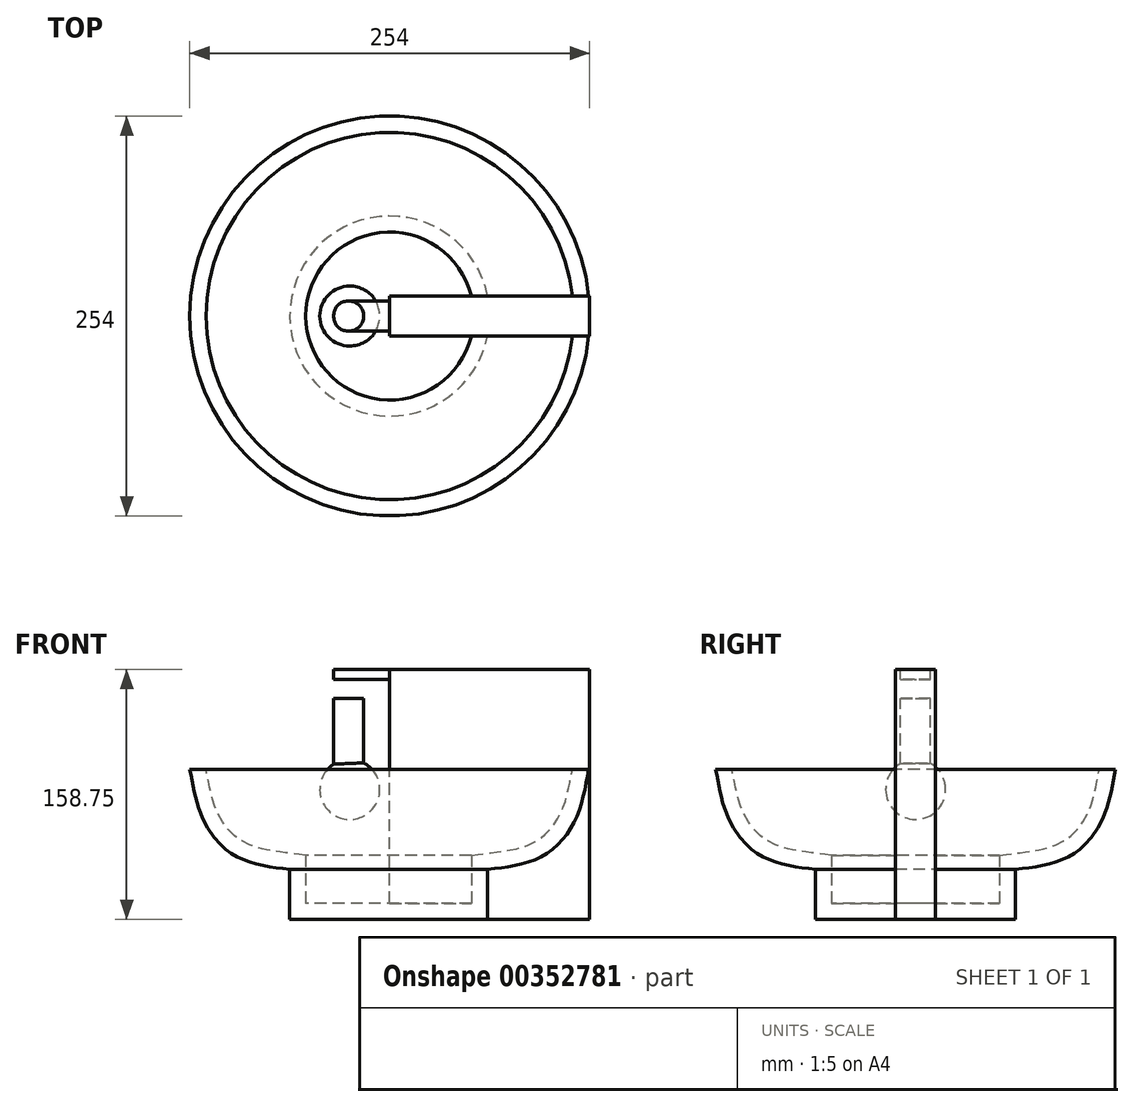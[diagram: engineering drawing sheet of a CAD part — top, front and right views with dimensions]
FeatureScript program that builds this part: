
annotation { "Feature Type Name" : "Feature", "Feature Type Description" : "" }
export const myFeature = defineFeature(function(context is Context, id is Id, definition is map)
    precondition{}
    {
        {
            var Q0;
            Q0=qCreatedBy(makeId("Top.planeOp"),FACE);
            cPlane(context, id + "F0", {"entities" : qUnion([Q0]), "cplaneType" : CPlaneType.OFFSET, "offset" : 95.25 * mm, "oppositeDirection" : true, "width" : 152.4 * mm, "height" : 152.4 * mm});
        }
        {
            var Q0;
            Q0=qCreatedBy(id+"F0.planeOp",FACE);
            var sketch = newSketch(context, id + "F1", { "sketchPlane" : qUnion([Q0])});
            skCircle(sketch, "E0", {"center": v(0, 0) * mm, "radius": 63.5 * mm});
            skSolve(sketch);
        }
        {
            var Q0;
            Q0=qCreatedBy(id+"F0.planeOp",FACE);
            cPlane(context, id + "F2", {"entities" : qUnion([Q0]), "cplaneType" : CPlaneType.OFFSET, "offset" : 31.75 * mm, "width" : 152.4 * mm, "height" : 152.4 * mm});
        }
        {
            var Q0;
            Q0=makeQuery(id+"F1.imprint","IMPRINT",FACE,{"disambiguationData":[TD([[makeQuery(id+"F1.imprint","IMPRINT",EDGE,{"derivedFrom":sQuery(id+"F1.wireOp",EDGE,"E0")}),1.0]])]});
            extrude(context, id + "F3", {"entities" : qUnion([Q0]), "depth" : 31.75 * mm});
        }
        {
            var Q0;
            Q0=qCreatedBy(makeId("Front.planeOp"),FACE);
            var sketch = newSketch(context, id + "F4", { "sketchPlane" : qUnion([Q0])});
            skLineSegment(sketch, "E1", {"start": v(0, 0) * mm, "end": v(0, -63.5) * mm});
            skLineSegment(sketch, "E2", {"start": v(0, -63.5) * mm, "end": v(-63.5, -63.5) * mm});
            skFitSpline(sketch, "E3", {"points": [v(-63.5, -63.5) * mm, v(-97, -55.41) * mm, v(-118.18, -32.67) * mm, v(-127, 0) * mm], "startDerivative": vector(-104.98, 12.82) * mm, "endDerivative": vector(-18.87, 100.94) * mm});
            skLineSegment(sketch, "E4", {"start": v(-127, 0) * mm, "end": v(0, 0) * mm});
            skSolve(sketch);
        }
        {
            var Q0;
            Q0=makeQuery(id+"F4.imprint","IMPRINT",FACE,{"disambiguationData":[TD([[makeQuery(id+"F4.imprint","IMPRINT",EDGE,{"derivedFrom":sQuery(id+"F4.wireOp",EDGE,"E1")}),-1.0]])]});
            var Q1;
            Q1=sQuery(id+"F4.wireOp",EDGE,"E1");
            revolve(context, id + "F5", {"operationType" : NewBodyOperationType.ADD, "entities" : qUnion([Q0]), "axis" : qUnion([Q1]), "revolveType" : RevolveType.FULL});
        }
        {
            var Q0;
            Q0=makeQuery(id+"F5.opRevolve","SWEPT_FACE",FACE,{"disambiguationData":[OSD([sQuery(id+"F4.wireOp",EDGE,"E4")])]});
            shell(context, id + "F6", {"entities" : qUnion([Q0]), "thickness" : 10.16 * mm});
        }
        {
            var Q0;
            Q0=qCreatedBy(makeId("Front.planeOp"),FACE);
            var sketch = newSketch(context, id + "F7", { "sketchPlane" : qUnion([Q0])});
            skLineSegment(sketch, "E5", {"start": v(0, 0) * mm, "end": v(127, 0) * mm});
            skLineSegment(sketch, "E6", {"start": v(127, 0) * mm, "end": v(127, -95.25) * mm});
            skLineSegment(sketch, "E7", {"start": v(127, -95.25) * mm, "end": v(0, -95.25) * mm});
            skLineSegment(sketch, "E8", {"start": v(0, -95.25) * mm, "end": v(0, 0) * mm});
            skSolve(sketch);
        }
        {
            var Q0;
            Q0=makeQuery(id+"F7.imprint","IMPRINT",FACE,{"disambiguationData":[TD([[makeQuery(id+"F7.imprint","IMPRINT",EDGE,{"derivedFrom":sQuery(id+"F7.wireOp",EDGE,"E5")}),-1.0]])]});
            extrude(context, id + "F8", {"entities" : qUnion([Q0]), "operationType" : NewBodyOperationType.ADD, "depth" : 12.7 * mm, "hasSecondDirection" : true, "secondDirectionOppositeDirection" : true, "secondDirectionDepth" : 12.7 * mm});
        }
        {
            var Q0;
            Q0=qCreatedBy(makeId("Top.planeOp"),FACE);
            var sketch = newSketch(context, id + "F9", { "sketchPlane" : qUnion([Q0])});
            skCircle(sketch, "E9", {"center": v(-26.04, 0) * mm, "radius": 9.53 * mm});
            skSolve(sketch);
        }
        {
            var Q0;
            Q0=qCreatedBy(makeId("Front.planeOp"),FACE);
            var sketch = newSketch(context, id + "F10", { "sketchPlane" : qUnion([Q0])});
            skLineSegment(sketch, "E10", {"start": v(0, 78.1) * mm, "end": v(0, -73.87) * mm, "construction": true});
            skLineSegment(sketch, "E11", {"start": v(-25.4, -18.53) * mm, "end": v(-25.4, 44.97) * mm});
            skSolve(sketch);
        }
        {
            var Q0;
            Q0=makeQuery(id+"F9.imprint","IMPRINT",FACE,{"disambiguationData":[TD([[makeQuery(id+"F9.imprint","IMPRINT",EDGE,{"derivedFrom":sQuery(id+"F9.wireOp",EDGE,"E9")}),1.0]])]});
            var Q1;
            Q1=sQuery(id+"F10.wireOp",EDGE,"E11");
            sweep(context, id + "F11", {"profiles" : qUnion([Q0]), "path" : qUnion([Q1])});
        }
        {
            var Q0;
            Q0=qCreatedBy(makeId("Front.planeOp"),FACE);
            var sketch = newSketch(context, id + "F12", { "sketchPlane" : qUnion([Q0])});
            skLineSegment(sketch, "E12", {"start": v(-25.4, 0) * mm, "end": v(-25.4, -25.4) * mm});
            skCircle(sketch, "E13", {"center": v(-25.4, -12.7) * mm, "radius": 19.05 * mm});
            skSolve(sketch);
        }
        {
            var Q0;
            Q0 = qSketchRegion(id + "F12", true);
            extrude(context, id + "F13", {"entities" : qUnion([Q0]), "operationType" : NewBodyOperationType.ADD, "depth" : 19.05 * mm, "hasSecondDirection" : true, "secondDirectionOppositeDirection" : true, "secondDirectionDepth" : 19.05 * mm});
        }
        {
            var Q0;
            Q0=makeQuery(id+"F13.opExtrude","CAP_FACE",FACE,{"disambiguationData":[OSD([sQuery(id+"F12.wireOp",EDGE,"E13")])],"isStart":false});
            fillet(context, id + "F14", {"entities" : qUnion([Q0]), "radius" : 19.05 * mm, "tangentPropagation" : true, "allowEdgeOverflow" : false});
        }
        {
            var Q0;
            Q0=makeQuery(id+"F13.opExtrude","CAP_EDGE",EDGE,{"disambiguationData":[OSD([sQuery(id+"F12.wireOp",EDGE,"E13")])],"isStart":true});
            fillet(context, id + "F15", {"entities" : qUnion([Q0]), "radius" : 19.05 * mm, "tangentPropagation" : true, "allowEdgeOverflow" : false});
        }
        {
            var Q0;
            Q0=qCreatedBy(makeId("Front.planeOp"),FACE);
            var sketch = newSketch(context, id + "F16", { "sketchPlane" : qUnion([Q0])});
            skLineSegment(sketch, "E14", {"start": v(0, 0) * mm, "end": v(0, 63.5) * mm});
            skLineSegment(sketch, "E15", {"start": v(0, 63.5) * mm, "end": v(127, 63.5) * mm});
            skLineSegment(sketch, "E16", {"start": v(127, 63.5) * mm, "end": v(127, 0) * mm});
            skLineSegment(sketch, "E17", {"start": v(127, 0) * mm, "end": v(0, 0) * mm});
            skSolve(sketch);
        }
        {
            var Q0;
            Q0=makeQuery(id+"F16.imprint","IMPRINT",FACE,{"disambiguationData":[TD([[makeQuery(id+"F16.imprint","IMPRINT",EDGE,{"derivedFrom":sQuery(id+"F16.wireOp",EDGE,"E14")}),-1.0]])]});
            extrude(context, id + "F17", {"entities" : qUnion([Q0]), "operationType" : NewBodyOperationType.ADD, "depth" : 12.7 * mm, "hasSecondDirection" : true, "secondDirectionOppositeDirection" : true, "secondDirectionDepth" : 12.7 * mm});
        }
        {
            var Q0;
            Q0=qCreatedBy(makeId("Front.planeOp"),FACE);
            var sketch = newSketch(context, id + "F18", { "sketchPlane" : qUnion([Q0])});
            skLineSegment(sketch, "E18", {"start": v(0, 0) * mm, "end": v(0, 63.5) * mm});
            skLineSegment(sketch, "E19", {"start": v(0, 63.5) * mm, "end": v(-35.56, 63.5) * mm});
            skLineSegment(sketch, "E20", {"start": v(-35.56, 63.5) * mm, "end": v(-35.56, 57.15) * mm});
            skLineSegment(sketch, "E21", {"start": v(-35.56, 57.15) * mm, "end": v(0, 57.15) * mm});
            skSolve(sketch);
        }
        {
            var Q0;
            {var subQ0=sQuery(id+"F18.wireOp",EDGE,"E19");Q0=makeQuery(id+"F18.imprint","IMPRINT",FACE,{"disambiguationData":[TD([[makeQuery(id+"F18.imprint","IMPRINT",EDGE,{"derivedFrom":subQ0}),1.0]])]});}
            extrude(context, id + "F19", {"entities" : qUnion([Q0]), "depth" : 9.52 * mm, "hasSecondDirection" : true, "secondDirectionOppositeDirection" : true, "secondDirectionDepth" : 9.52 * mm});
        }
        {
            var Q0;
            Q0=makeQuery(id+"F19.opExtrude","CAP_EDGE",EDGE,{"disambiguationData":[OSD([sQuery(id+"F18.wireOp",EDGE,"E20")])],"isStart":false});
            fillet(context, id + "F20", {"entities" : qUnion([Q0]), "radius" : 8.9 * mm, "tangentPropagation" : true, "allowEdgeOverflow" : false});
        }
        {
            var Q0;
            Q0=makeQuery(id+"F19.opExtrude","CAP_EDGE",EDGE,{"disambiguationData":[OSD([sQuery(id+"F18.wireOp",EDGE,"E20")])],"isStart":true});
            fillet(context, id + "F21", {"entities" : qUnion([Q0]), "radius" : 8.9 * mm, "tangentPropagation" : true, "allowEdgeOverflow" : false});
        }
    });
